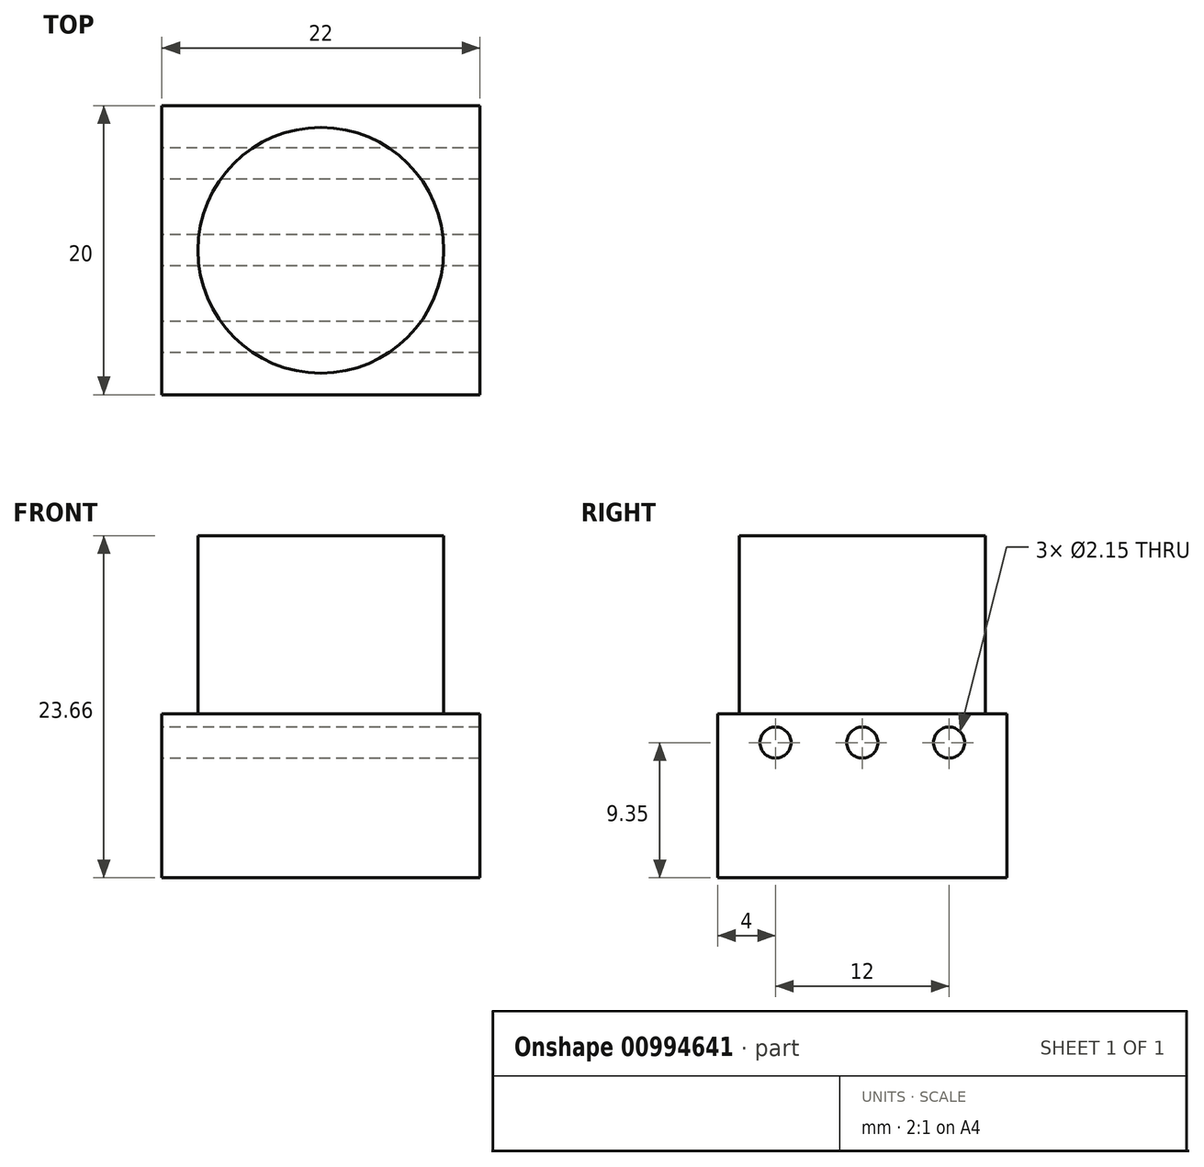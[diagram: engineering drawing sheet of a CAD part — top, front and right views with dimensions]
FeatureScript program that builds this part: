
annotation { "Feature Type Name" : "Feature", "Feature Type Description" : "" }
export const myFeature = defineFeature(function(context is Context, id is Id, definition is map)
    precondition{}
    {
        {
            var Q0;
            Q0=qCreatedBy(makeId("Top.planeOp"),FACE);
            var sketch = newSketch(context, id + "F0", { "sketchPlane" : qUnion([Q0])});
            skLineSegment(sketch, "E0.bottom", {"start": v(-11, 10) * mm, "end": v(11, 10) * mm});
            skLineSegment(sketch, "E0.top", {"start": v(-11, -10) * mm, "end": v(11, -10) * mm});
            skLineSegment(sketch, "E0.left", {"start": v(-11, 10) * mm, "end": v(-11, -10) * mm});
            skLineSegment(sketch, "E0.right", {"start": v(11, 10) * mm, "end": v(11, -10) * mm});
            skPoint(sketch, "E1", {"position": v(0, 10) * mm});
            skPoint(sketch, "E2", {"position": v(-11, 0) * mm});
            skSolve(sketch);
        }
        {
            var Q0;
            Q0=makeQuery(id+"F0.imprint","IMPRINT",FACE,{"disambiguationData":[TD([[makeQuery(id+"F0.imprint","IMPRINT",EDGE,{"derivedFrom":sQuery(id+"F0.wireOp",EDGE,"E0.bottom")}),-1.0]])]});
            extrude(context, id + "F1", {"entities" : qUnion([Q0]), "depth" : 11.35 * mm, "offsetDistance" : 25 * mm});
        }
        {
            var Q0;
            Q0=makeQuery(id+"F1.opExtrude","SWEPT_FACE",FACE,{"disambiguationData":[OSD([sQuery(id+"F0.wireOp",EDGE,"E0.left")])]});
            var sketch = newSketch(context, id + "F2", { "sketchPlane" : qUnion([Q0])});
            skLineSegment(sketch, "E3", {"start": v(6, 9.35) * mm, "end": v(-6, 9.35) * mm, "construction": true});
            skCircle(sketch, "E4", {"center": v(-6, 9.35) * mm, "radius": 1.07 * mm});
            skCircle(sketch, "E5", {"center": v(0, 9.35) * mm, "radius": 1.07 * mm});
            skCircle(sketch, "E6", {"center": v(6, 9.35) * mm, "radius": 1.07 * mm});
            skSolve(sketch);
        }
        {
            var Q0;
            Q0 = qSketchRegion(id + "F2", true);
            extrude(context, id + "F3", {"entities" : qUnion([Q0]), "operationType" : NewBodyOperationType.REMOVE, "endBound" : BoundingType.THROUGH_ALL, "oppositeDirection" : true, "depth" : 25 * mm, "offsetDistance" : 25 * mm});
        }
        {
            var Q0;
            Q0=makeQuery(id+"F1.opExtrude","CAP_FACE",FACE,{"disambiguationData":[OSD([sQuery(id+"F0.wireOp",EDGE,"E0.bottom"),sQuery(id+"F0.wireOp",EDGE,"E0.top"),sQuery(id+"F0.wireOp",EDGE,"E0.left"),sQuery(id+"F0.wireOp",EDGE,"E0.right")])],"isStart":false});
            var sketch = newSketch(context, id + "F4", { "sketchPlane" : qUnion([Q0])});
            skCircle(sketch, "E7", {"center": v(0, 0) * mm, "radius": 8.5 * mm});
            skSolve(sketch);
        }
        {
            var Q0;
            Q0 = qSketchRegion(id + "F4", true);
            extrude(context, id + "F5", {"entities" : qUnion([Q0]), "operationType" : NewBodyOperationType.ADD, "depth" : 12.3 * mm, "offsetDistance" : 25 * mm});
        }
    });
